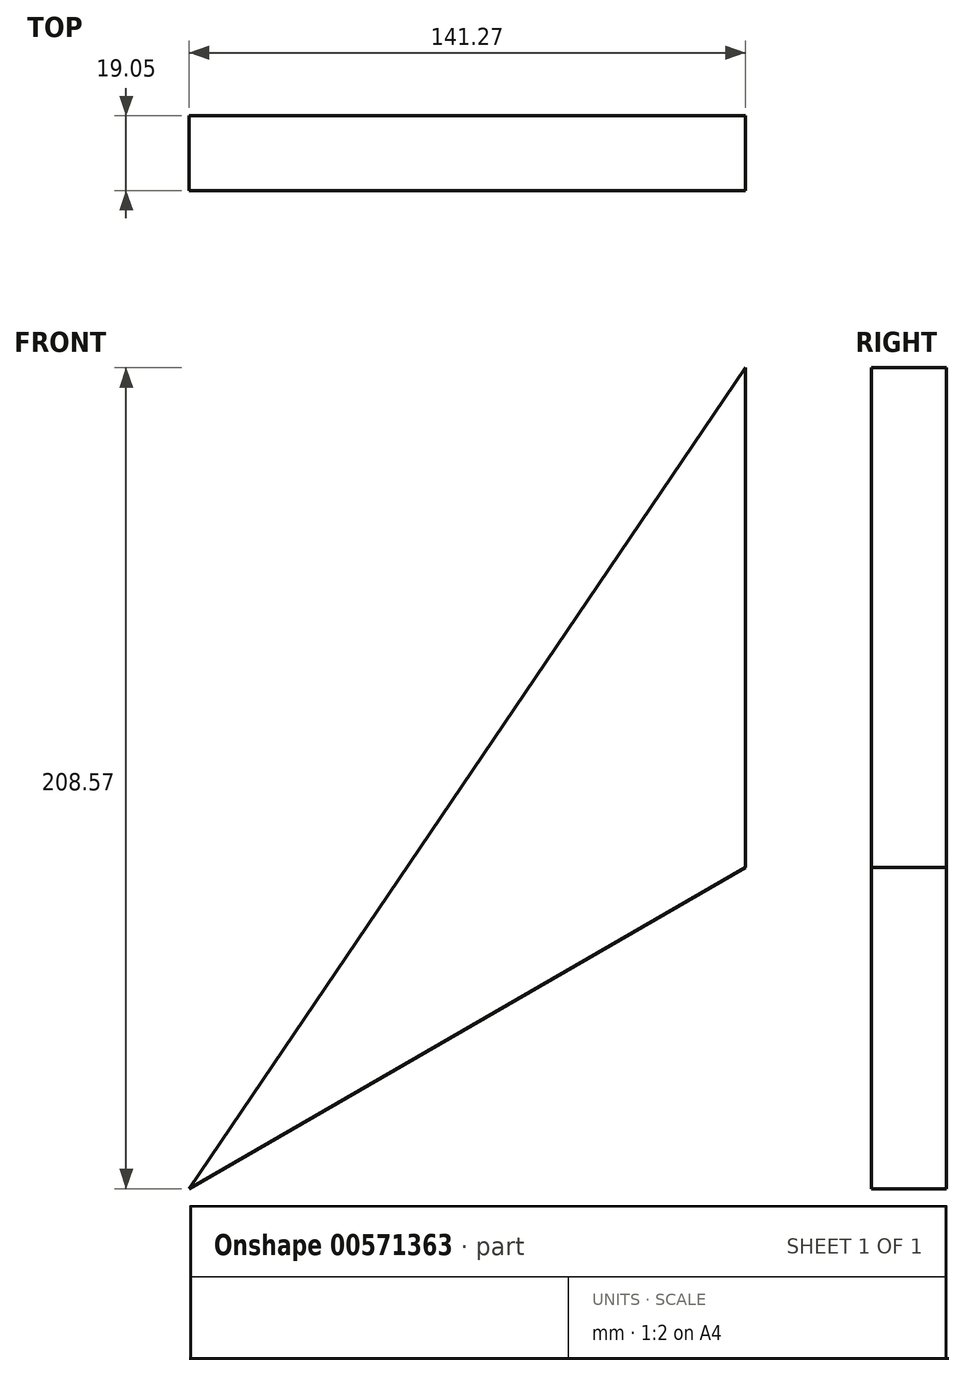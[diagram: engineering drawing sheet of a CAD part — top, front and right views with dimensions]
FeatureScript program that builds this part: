
annotation { "Feature Type Name" : "Feature", "Feature Type Description" : "" }
export const myFeature = defineFeature(function(context is Context, id is Id, definition is map)
    precondition{}
    {
        {
            var Q0;
            Q0=qCreatedBy(makeId("Front.planeOp"),FACE);
            var sketch = newSketch(context, id + "F0", { "sketchPlane" : qUnion([Q0])});
            skLineSegment(sketch, "E0", {"start": v(-141.27, 15.61) * mm, "end": v(0, 224.18) * mm});
            skLineSegment(sketch, "E1", {"start": v(0, 224.18) * mm, "end": v(0, 97.18) * mm});
            skLineSegment(sketch, "E2", {"start": v(0, 97.18) * mm, "end": v(-141.27, 15.61) * mm});
            skSolve(sketch);
        }
        {
            var Q0;
            Q0 = qSketchRegion(id + "F0", true);
            extrude(context, id + "F1", {"entities" : qUnion([Q0]), "depth" : 19.05 * mm, "offsetDistance" : 25.4 * mm});
        }
    });
